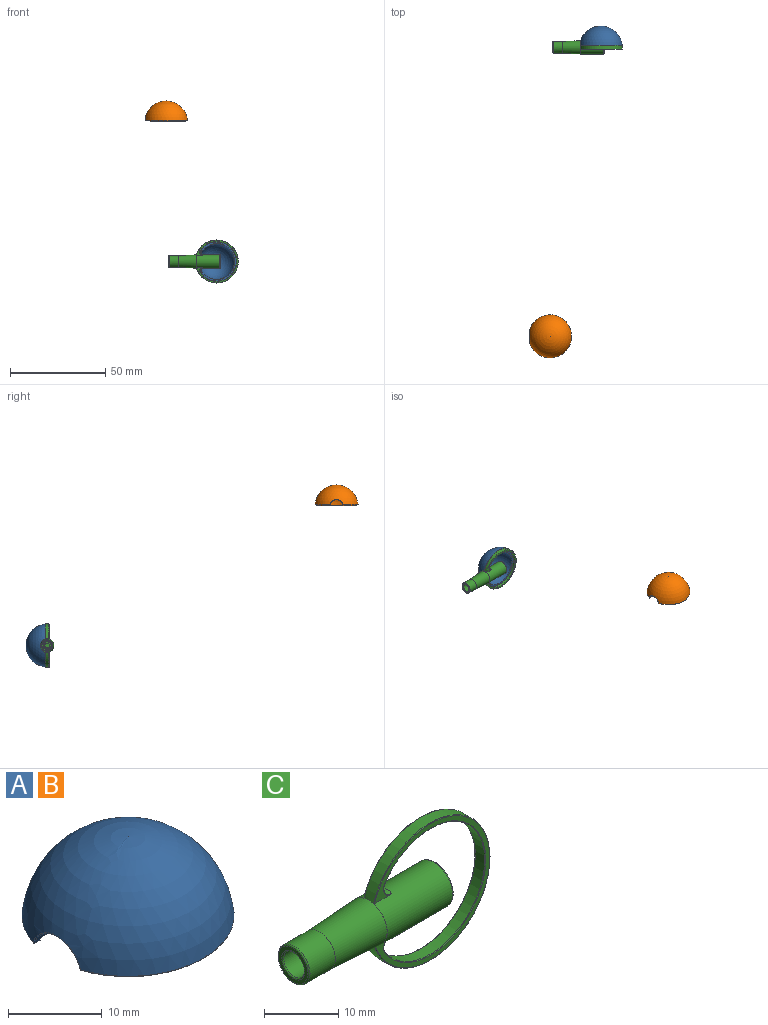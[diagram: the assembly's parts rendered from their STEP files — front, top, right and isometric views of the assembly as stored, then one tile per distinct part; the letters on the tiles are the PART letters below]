
ASSEMBLY  parts=3 mates=1
PART A: 17 faces, bbox 23.8x24.4x10.9 mm
  f0: cylinder r=10.34mm len=20.68mm, axis (0,0,-1), area 19.4mm2, adj f5,f8,f12,f15
  f1: plane 20.48x18.33mm, normal (0,0,-1), area 40.7mm2, adj f6,f8,f12,f15
  f2: cylinder r=3.6mm len=6.92mm, axis (1,0,0), area 16.7mm2, adj f5,f7,f10,f11,f13,f14,f16
  f3: sphere r=9.34mm, area 493.4mm2, adj f6,f7,f12,f13,f15,f16
  f4: sphere r=11.34mm, area 714.7mm2, adj f9,f10
  f5: plane 22.37x21.82mm, normal (0,0,-1), area 51.3mm2, adj f0,f2,f9,f10,f11,f14
  f6: torus R=9.42mm, axis (0,0,1), area 7.3mm2, adj f1,f3,f12,f15
  f7: torus R=3.7mm, axis (1,0,0), area 1mm2, adj f2,f3,f13,f16
  f8: torus R=10.24mm, axis (0,0,1), area 7.7mm2, adj f0,f1,f12,f15
  f9: torus R=11.19mm, axis (0,0,1), area 10.6mm2, adj f4,f5,f10
  f10: torus R=3.7mm, axis (1,0,0), area 1.8mm2, adj f2,f4,f5,f9
  f11: cylinder r=10.34mm len=4.11mm, axis (0,0,-1), area 2.4mm2, adj f2,f5,f12,f13
  f12: cylinder r=2.85mm len=2.79mm, axis (0,0,-1), area 2.9mm2, adj f0,f1,f3,f6,f8,f11,f13
  f13: plane 4.13x2.58mm, normal (0,0,-1), area 3mm2, adj f2,f3,f7,f11,f12
  f14: cylinder r=10.34mm len=4.11mm, axis (0,0,-1), area 2.4mm2, adj f2,f5,f15,f16
  f15: cylinder r=2.85mm len=2.79mm, axis (0,0,-1), area 2.9mm2, adj f0,f1,f3,f6,f8,f14,f16
  f16: plane 4.13x2.58mm, normal (0,0,-1), area 3mm2, adj f2,f3,f7,f14,f15
PART B: same geometry as A
PART C: 38 faces, bbox 124.8x61.7x61.7 mm
  f0: plane 22.41x21.89mm, normal (0,1,0), area 49.6mm2, adj f2,f11,f14,f21,f22,f23,f27
  f1: plane 22.41x21.89mm, normal (0,-1,0), area 49.6mm2, adj f2,f12,f13,f24,f25,f26,f28
  f2: cylinder r=3.5mm len=12.43mm, axis (1,0,0), area 260.4mm2, adj f0,f1,f11,f12,f13,f14,f19,f20
  f3: torus R=90.83mm, axis (1,0,0), area 186.3mm2, adj f9,f11,f12,f18,f31,f32,f33,f34
  f4: cylinder r=2mm len=14.8mm, axis (1,0,0), area 185.9mm2, adj f5,f16,f17,f29,f30,f37
  f5: plane 4x4mm, normal (-1,0,0), area 7.7mm2, adj f4,f6
  f6: cylinder r=1.25mm len=10mm, axis (1,0,0), area 78.5mm2, adj f5,f7
  f7: plane 2.5x2.5mm, normal (-1,0,0), area 4.9mm2, adj f6
  f8: plane 6.6x6.6mm, normal (1,0,0), area 34.2mm2, adj f35
  f9: cylinder r=3mm len=6mm, axis (1,0,0), area 90.5mm2, adj f3,f36
  f10: plane 5.6x5.6mm, normal (-1,0,0), area 9.4mm2, adj f36,f37
  f11: plane 0.82x0.58mm, normal (0,0,1), area 0.4mm2, adj f0,f2,f3,f14,f18,f27,f34
  f12: plane 0.82x0.58mm, normal (0,0,1), area 0.4mm2, adj f1,f2,f3,f13,f18,f28,f31
  f13: plane 0.79x0.14mm, normal (-1,0,0), area 0mm2, adj f1,f2,f12
  f14: plane 0.79x0.14mm, normal (-1,0,0), area 0mm2, adj f0,f2,f11
  f15: cylinder r=10.34mm len=20.68mm, axis (0,1,0), area 94.7mm2, adj f19,f20,f22,f25
  f16: plane 2x0.54mm, normal (-1,0,0), area 0.8mm2, adj f4,f17,f29,f30
  f17: cylinder r=10.34mm len=1.8mm, axis (0,1,0), area 0.7mm2, adj f4,f16,f29,f30
  f18: sphere r=11.34mm, area 116.5mm2, adj f3,f11,f12,f27,f28
  f19: bspline ~4.13x2.85mm, area 5.4mm2, adj f2,f15,f21,f24
  f20: bspline ~4.13x2.85mm, area 5.4mm2, adj f2,f15,f23,f26
  f21: bspline ~2.71x1.74mm, area 0.4mm2, adj f0,f2,f19,f22
  f22: torus R=10.44mm, axis (0,-1,0), area 8.3mm2, adj f0,f15,f21,f23
  f23: bspline ~2.71x1.74mm, area 0.4mm2, adj f0,f2,f20,f22
  f24: bspline ~2.71x1.74mm, area 0.4mm2, adj f1,f2,f19,f25
  f25: torus R=10.44mm, axis (0,-1,0), area 8.3mm2, adj f1,f15,f24,f26
  f26: bspline ~2.71x1.74mm, area 0.4mm2, adj f1,f2,f20,f25
  f27: torus R=11.2mm, axis (0,-1,0), area 9.5mm2, adj f0,f2,f11,f18,f33
  f28: torus R=11.2mm, axis (0,-1,0), area 9.5mm2, adj f1,f2,f12,f18,f32
  f29: torus R=10.44mm, axis (0,-1,0), area 0mm2, adj f4,f16,f17
  f30: torus R=10.44mm, axis (0,-1,0), area 0mm2, adj f4,f16,f17
  f31: torus R=3.3mm, axis (-1,0,0), area 0.2mm2, adj f2,f3,f12,f32
  f32: bspline ~0.05x0.03mm, area 0mm2, adj f3,f28,f31
  f33: bspline ~0.05x0.03mm, area 0mm2, adj f3,f27,f34
  f34: torus R=3.3mm, axis (-1,0,0), area 0.2mm2, adj f2,f3,f11,f33
  f35: torus R=3.3mm, axis (-1,0,0), area 6.8mm2, adj f2,f8
  f36: torus R=2.8mm, axis (-1,0,0), area 5.8mm2, adj f9,f10
  f37: torus R=2.2mm, axis (-1,0,0), area 4.1mm2, adj f4,f10
PLACE A rot(axis=(-1,0,0),90deg) t=(-13.53,-12.33,-0.73)mm
PLACE B t=(-40.12,-163.96,72.2)mm
PLACE C t=(-13.53,-12.13,-0.73)mm
MATE fastened A.f9 <-> C.f27  axis (0,-1,0) through (-13.53,-11.22,-0.73)mm
